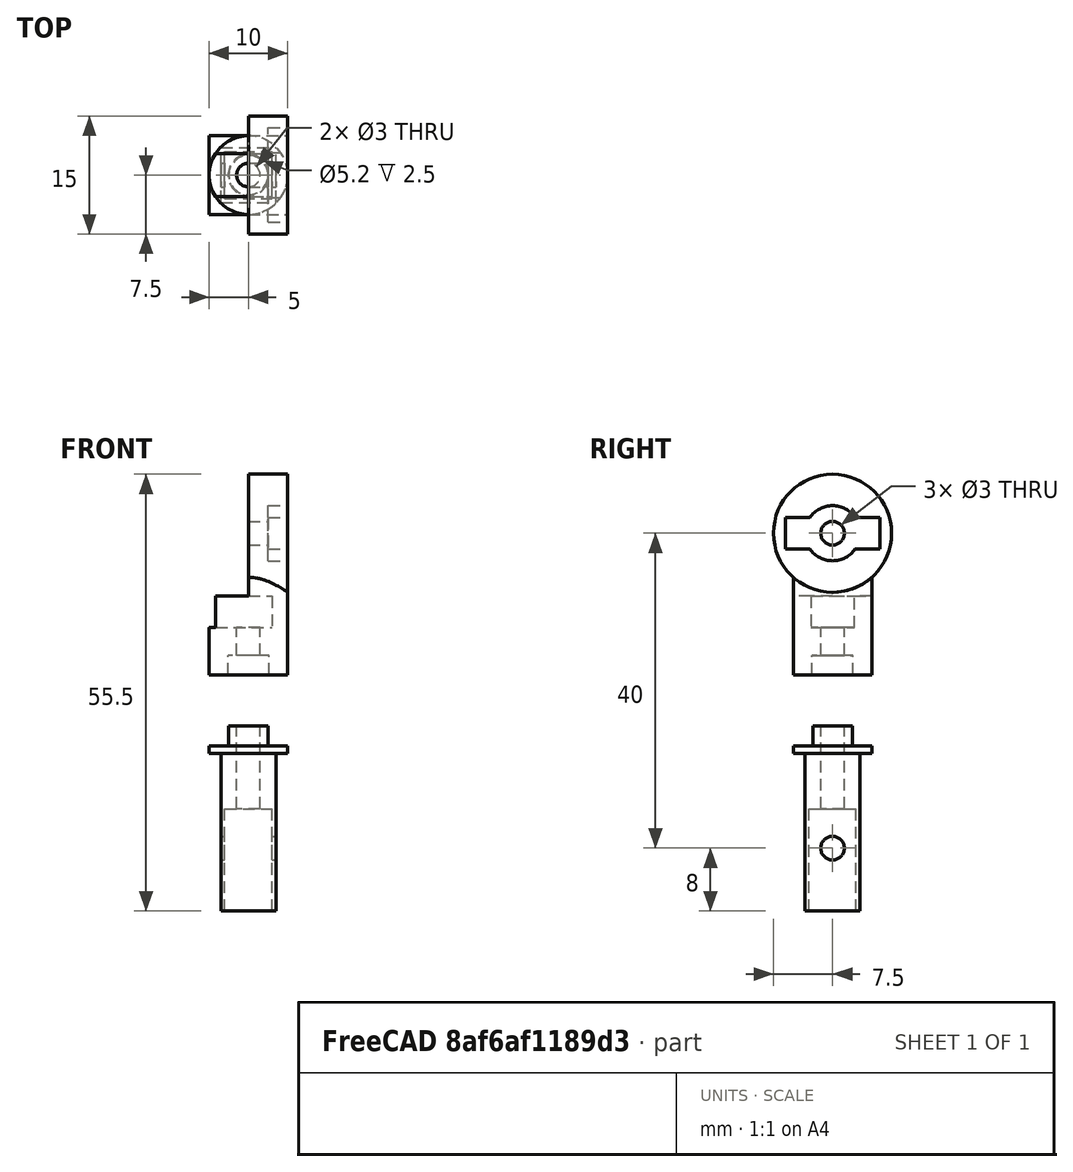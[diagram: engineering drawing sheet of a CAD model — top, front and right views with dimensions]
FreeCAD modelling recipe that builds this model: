
FCSTD DOCUMENT  (FreeCAD 0.17RUnknown)
Label: 2wayjoint
License: All rights reserved
LicenseURL: http://en.wikipedia.org/wiki/All_rights_reserved
objects: Part::Cylinder×12, Part::Cut×11, Part::Box×7, Part::MultiFuse×5
note: 35 computed .brp shape members not serialized (recipe doc carries the construction recipe); baked Part::Feature solids carry a one-line shape summary decoded from their .brp

FEATURE [Part::Box] Box  label="Würfel"
  AttacherType = Attacher::AttachEngine3D
  Height = 1
  Length = 10
  Placement = pos=(-5,-5,-10) rot=(0,0,1;0rad)
  Width = 10
FEATURE [Part::Cylinder] Cylinder  label="Zylinder"
  Angle = 360
  AttacherType = Attacher::AttachEngine3D
  Height = 2.5
  Placement = pos=(0,0,-9) rot=(0,0,1;0rad)
  Radius = 2.5
FEATURE [Part::Box] Box001  label="Würfel001"
  AttacherType = Attacher::AttachEngine3D
  Height = 20
  Length = 7
  Placement = pos=(-3.5,-3.5,-30) rot=(0,0,1;0rad)
  Width = 7
FEATURE [Part::MultiFuse] Fusion001
  Shapes = -> [Box,Cylinder,Box001]
FEATURE [Part::Box] Box003  label="Würfel003"
  AttacherType = Attacher::AttachEngine3D
  Height = 13
  Length = 6
  Placement = pos=(-3,-3,-30) rot=(0,0,1;0rad)
  Width = 6
FEATURE [Part::Cut] Cut
  Base = -> Fusion001
  Tool = -> Box003
FEATURE [Part::Cylinder] Cylinder001  label="Zylinder001"
  Angle = 360
  AttacherType = Attacher::AttachEngine3D
  Height = 12
  Placement = pos=(0,0,-18) rot=(0,0,1;0rad)
  Radius = 1.5
FEATURE [Part::Cut] Cut001
  Base = -> Cut
  Tool = -> Cylinder001
FEATURE [Part::Cylinder] Cylinder002  label="Zylinder002"
  Angle = 360
  AttacherType = Attacher::AttachEngine3D
  Height = 0.5
  Placement = pos=(3,0,-22) rot=(0,1,0;1.5708rad)
  Radius = 1.5
FEATURE [Part::Cylinder] Cylinder003  label="Zylinder003"
  Angle = 360
  AttacherType = Attacher::AttachEngine3D
  Height = 0.5
  Placement = pos=(-3.5,0,-22) rot=(0,1,0;1.5708rad)
  Radius = 1.5
FEATURE [Part::Cut] Cut002
  Base = -> Cut001
  Tool = -> Cylinder002
FEATURE [Part::Cut] Cut003  label="Bottom"
  Base = -> Cut002
  Tool = -> Cylinder003
FEATURE [Part::Cylinder] Cylinder004  label="Zylinder004"
  Angle = 360
  AttacherType = Attacher::AttachEngine3D
  Height = 10
  Radius = 5
FEATURE [Part::Cylinder] Cylinder005  label="Zylinder005"
  Angle = 360
  AttacherType = Attacher::AttachEngine3D
  Height = 2.5
  Radius = 2.6
FEATURE [Part::Cut] Cut004
  Base = -> Cylinder004
  Tool = -> Cylinder005
FEATURE [Part::Cylinder] Cylinder007  label="Zylinder007"
  Angle = 360
  AttacherType = Attacher::AttachEngine3D
  Height = 5
  Placement = pos=(0,0,2.5) rot=(0,0,1;0rad)
  Radius = 1.5
FEATURE [Part::Cylinder] Cylinder008  label="Zylinder008"
  Angle = 360
  AttacherType = Attacher::AttachEngine3D
  Height = 5
  Placement = pos=(0,0,18) rot=(0,1,0;1.5708rad)
  Radius = 7.5
FEATURE [Part::Cylinder] Cylinder009  label="Zylinder009"
  Angle = 180
  AttacherType = Attacher::AttachEngine3D
  Height = 3
  Placement = pos=(0,0,10) rot=(0,0,-1;1.5708rad)
  Radius = 5
FEATURE [Part::Cylinder] Cylinder011  label="Zylinder011"
  Angle = 360
  AttacherType = Attacher::AttachEngine3D
  Height = 5
  Placement = pos=(0,0,18) rot=(0,1,0;1.5708rad)
  Radius = 1.5
FEATURE [Part::Cylinder] Cylinder012  label="Zylinder012"
  Angle = 360
  AttacherType = Attacher::AttachEngine3D
  Height = 2.5
  Placement = pos=(2.5,0,18) rot=(0,1,0;1.5708rad)
  Radius = 3.5
FEATURE [Part::Cut] Cut008
  Base = -> Cylinder008
  Tool = -> Cylinder011
FEATURE [Part::Cut] Cut009
  Base = -> Cut004
  Tool = -> Cylinder007
FEATURE [Part::Cut] Cut010
  Base = -> Cut008
  Tool = -> Cylinder012
FEATURE [Part::Cylinder] Cylinder013  label="Zylinder013"
  Angle = 360
  AttacherType = Attacher::AttachEngine3D
  Height = 4
  Placement = pos=(0,17,0) rot=(0,0,1;0rad)
  Radius = 5
FEATURE [Part::Box] Box004  label="Würfel004"
  AttacherType = Attacher::AttachEngine3D
  Height = 4
  Length = 10
  Placement = pos=(-5,19.75,0) rot=(0,0,1;0rad)
  Width = 2.25
FEATURE [Part::Box] Box005  label="Würfel005"
  AttacherType = Attacher::AttachEngine3D
  Height = 4
  Length = 10
  Placement = pos=(-5,12,0) rot=(0,0,1;0rad)
  Width = 2.25
FEATURE [Part::Box] Box006  label="Würfel006"
  AttacherType = Attacher::AttachEngine3D
  Height = 4
  Length = 1.99
  Placement = pos=(3.01,12,0) rot=(0,0,1;0rad)
  Width = 10
FEATURE [Part::MultiFuse] Fusion
  Shapes = -> [Box005,Box004]
FEATURE [Part::MultiFuse] Fusion002
  Shapes = -> [Fusion,Box006]
FEATURE [Part::Cut] Cut011
  Base = -> Cylinder013
  Placement = pos=(0,-17,6) rot=(0,0,1;0rad)
  Tool = -> Fusion002
FEATURE [Part::Cut] Cut012
  Base = -> Cut009
  Tool = -> Cut011
FEATURE [Part::MultiFuse] Fusion003
  Shapes = -> [Cut010,Cylinder009]
FEATURE [Part::MultiFuse] Fusion004  label="cut"
  Shapes = -> [Fusion003,Cut012]
FEATURE [Part::Box] Box007  label="Würfel007"
  AttacherType = Attacher::AttachEngine3D
  Height = 4
  Length = 2.5
  Placement = pos=(2.5,-6,16) rot=(0,0,1;0rad)
  Width = 12
FEATURE [Part::Cut] Cut013  label="top"
  Base = -> Fusion004
  Tool = -> Box007
